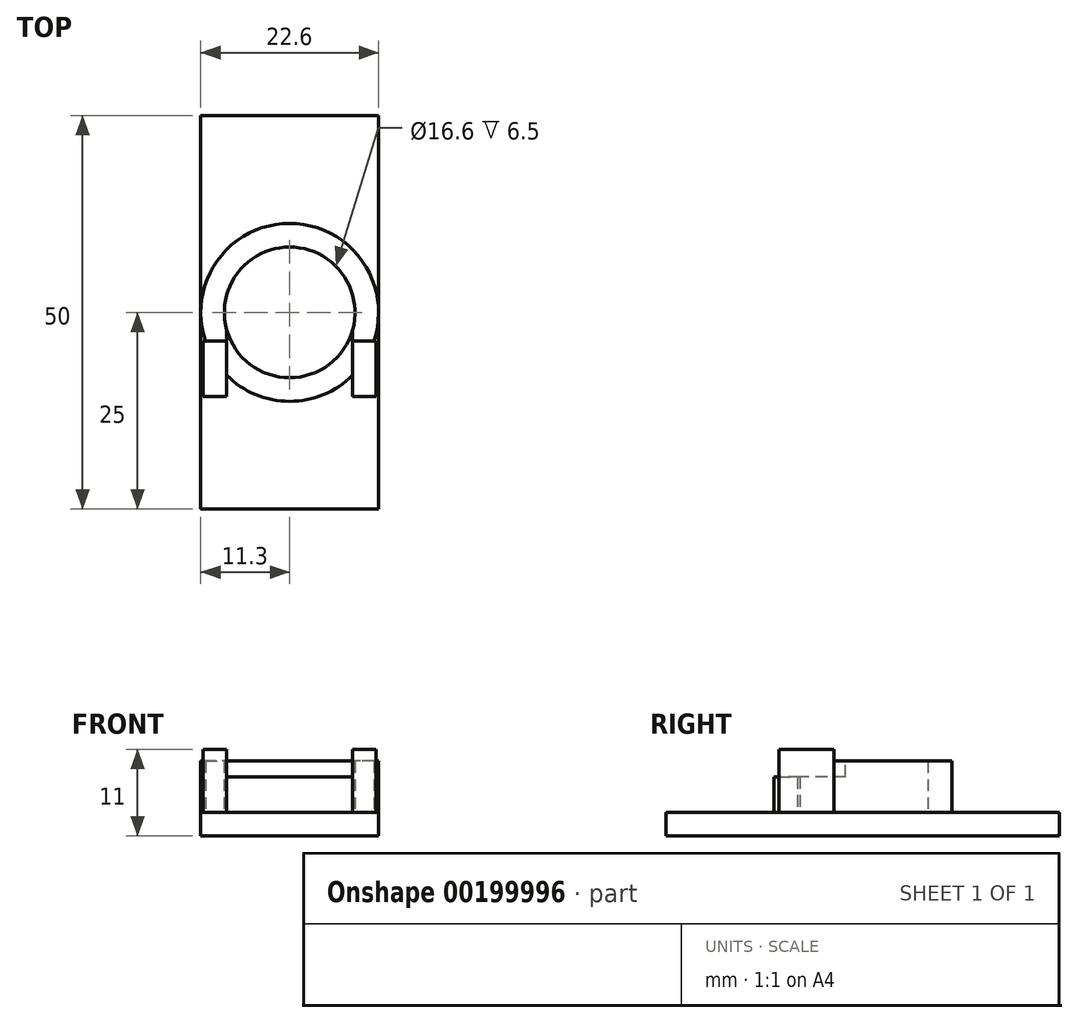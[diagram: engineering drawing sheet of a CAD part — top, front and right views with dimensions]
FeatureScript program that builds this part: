
annotation { "Feature Type Name" : "Feature", "Feature Type Description" : "" }
export const myFeature = defineFeature(function(context is Context, id is Id, definition is map)
    precondition{}
    {
        {
            var Q0;
            Q0=qCreatedBy(makeId("Top.planeOp"),FACE);
            var sketch = newSketch(context, id + "F0", { "sketchPlane" : qUnion([Q0])});
            skCircle(sketch, "E0", {"center": v(0, 0) * mm, "radius": 8.3 * mm});
            skCircle(sketch, "E1.0", {"center": v(0, 0) * mm, "radius": 11.3 * mm});
            skLineSegment(sketch, "E2.bottom", {"start": v(11.3, 25) * mm, "end": v(-11.3, 25) * mm});
            skLineSegment(sketch, "E2.top", {"start": v(11.3, -25) * mm, "end": v(-11.3, -25) * mm});
            skLineSegment(sketch, "E2.left", {"start": v(11.3, 25) * mm, "end": v(11.3, -25) * mm});
            skLineSegment(sketch, "E2.right", {"start": v(-11.3, 25) * mm, "end": v(-11.3, -25) * mm});
            skLineSegment(sketch, "E3.bottom", {"start": v(-11, -3.67) * mm, "end": v(-8, -3.67) * mm});
            skLineSegment(sketch, "E3.top", {"start": v(-11, -10.67) * mm, "end": v(-8, -10.67) * mm});
            skLineSegment(sketch, "E3.left", {"start": v(-11, -3.67) * mm, "end": v(-11, -10.67) * mm});
            skLineSegment(sketch, "E3.right", {"start": v(-8, -3.67) * mm, "end": v(-8, -10.67) * mm});
            skLineSegment(sketch, "E4", {"start": v(0, 0) * mm, "end": v(0, -25) * mm, "construction": true});
            skLineSegment(sketch, "E5.MirrorCS", {"start": v(11, -3.67) * mm, "end": v(8, -3.67) * mm});
            skLineSegment(sketch, "E6.MirrorCS", {"start": v(8, -3.67) * mm, "end": v(8, -10.67) * mm});
            skLineSegment(sketch, "E7.MirrorCS", {"start": v(11, -3.67) * mm, "end": v(11, -10.67) * mm});
            skLineSegment(sketch, "E8.MirrorCS", {"start": v(11, -10.67) * mm, "end": v(8, -10.67) * mm});
            skPoint(sketch, "E9", {"position": v(0, -11.3) * mm});
            skLineSegment(sketch, "E10", {"start": v(0, 0) * mm, "end": v(11.3, 0) * mm, "construction": true});
            skSolve(sketch);
        }
        {
            var Q0;
            Q0=makeQuery(id+"F0.imprint","IMPRINT",FACE,{"disambiguationData":[TD([[makeQuery(id+"F0.imprint","IMPRINT",EDGE,{"derivedFrom":sQuery(id+"F0.wireOp",EDGE,"E0")}),-1.0]])]});
            extrude(context, id + "F1", {"entities" : qUnion([Q0]), "depth" : 6.5 * mm});
        }
        {
            var Q0;
            {var subQ0=sQuery(id+"F0.wireOp",EDGE,"E6.MirrorCS");var subQ1=sQuery(id+"F0.wireOp",EDGE,"E1.0");var subQ2=makeQuery(id+"F0.imprint","INTERSECT",VERTEX,{"derivedFrom":[subQ1,subQ0]});Q0=makeQuery(id+"F0.imprint","IMPRINT",FACE,{"disambiguationData":[TD([[makeQuery(id+"F0.imprint","IMPRINT",EDGE,{"disambiguationData":[TD([[subQ2,-1.0]])],"derivedFrom":subQ1}),1.0]])]});}
            var Q1;
            {var subQ0=sQuery(id+"F0.wireOp",EDGE,"E7.MirrorCS");Q1=makeQuery(id+"F0.imprint","IMPRINT",FACE,{"disambiguationData":[TD([[makeQuery(id+"F0.imprint","IMPRINT",EDGE,{"derivedFrom":subQ0}),-1.0]])]});}
            var Q2;
            {var subQ0=sQuery(id+"F0.wireOp",EDGE,"E3.top");Q2=makeQuery(id+"F0.imprint","IMPRINT",FACE,{"disambiguationData":[TD([[makeQuery(id+"F0.imprint","IMPRINT",EDGE,{"derivedFrom":subQ0}),1.0]])]});}
            var Q3;
            {var subQ0=sQuery(id+"F0.wireOp",EDGE,"E3.bottom");var subQ1=sQuery(id+"F0.wireOp",EDGE,"E1.0");var subQ2=makeQuery(id+"F0.imprint","INTERSECT",VERTEX,{"derivedFrom":[subQ1,subQ0]});Q3=makeQuery(id+"F0.imprint","IMPRINT",FACE,{"disambiguationData":[TD([[makeQuery(id+"F0.imprint","IMPRINT",EDGE,{"disambiguationData":[TD([[subQ2,-1.0]])],"derivedFrom":subQ1}),1.0]])]});}
            extrude(context, id + "F2", {"entities" : qUnion([Q0, Q1, Q2, Q3]), "operationType" : NewBodyOperationType.ADD, "depth" : 8 * mm});
        }
        {
            var Q0;
            Q0=makeQuery(id+"F1.opExtrude","CAP_FACE",FACE,{"disambiguationData":[OSD([sQuery(id+"F0.wireOp",EDGE,"E0"),sQuery(id+"F0.wireOp",EDGE,"E1.0"),sQuery(id+"F0.wireOp",EDGE,"E3.bottom"),sQuery(id+"F0.wireOp",EDGE,"E3.right"),sQuery(id+"F0.wireOp",EDGE,"E5.MirrorCS"),sQuery(id+"F0.wireOp",EDGE,"E6.MirrorCS")])],"isStart":false});
            var sketch = newSketch(context, id + "F3", { "sketchPlane" : qUnion([Q0])});
            skLineSegment(sketch, "E11.0", {"start": v(-8, -3.67) * mm, "end": v(-8, -10.67) * mm});
            skLineSegment(sketch, "E12.0", {"start": v(8, -3.67) * mm, "end": v(8, -10.67) * mm});
            skLineSegment(sketch, "E13", {"start": v(-8, -10.67) * mm, "end": v(8, -10.67) * mm});
            skLineSegment(sketch, "E14", {"start": v(8, -3.67) * mm, "end": v(-8, -3.67) * mm});
            skLineSegment(sketch, "E15.top", {"start": v(-8, -11.3) * mm, "end": v(8, -11.3) * mm});
            skLineSegment(sketch, "E15.left", {"start": v(-8, -10.67) * mm, "end": v(-8, -11.3) * mm});
            skLineSegment(sketch, "E15.right", {"start": v(8, -10.67) * mm, "end": v(8, -11.3) * mm});
            skPoint(sketch, "E16.0", {"position": v(0, -11.3) * mm});
            skLineSegment(sketch, "E17.top", {"start": v(8, -2.21) * mm, "end": v(-8, -2.21) * mm});
            skLineSegment(sketch, "E17.left", {"start": v(8, -3.67) * mm, "end": v(8, -2.21) * mm});
            skLineSegment(sketch, "E17.right", {"start": v(-8, -3.67) * mm, "end": v(-8, -2.21) * mm});
            skSolve(sketch);
        }
        {
            var Q0;
            {var subQ0=sQuery(id+"F3.wireOp",EDGE,"E14");var subQ1=makeQuery(id+"F1.opExtrude","CAP_EDGE",EDGE,{"disambiguationData":[OSD([sQuery(id+"F0.wireOp",EDGE,"E0")])],"isStart":false});var subQ2=makeQuery(id+"F3.imprint","INTERSECT",VERTEX,{"disambiguationData":[OD(0.0)],"derivedFrom":[subQ1,subQ0]});Q0=makeQuery(id+"F3.imprint","IMPRINT",FACE,{"disambiguationData":[TD([[makeQuery(id+"F3.imprint","IMPRINT",EDGE,{"disambiguationData":[TD([[subQ2,-1.0]])],"derivedFrom":subQ0}),1.0]])]});}
            var Q1;
            {var subQ0=sQuery(id+"F3.wireOp",EDGE,"E14");var subQ3=makeQuery(id+"F1.opExtrude","CAP_EDGE",EDGE,{"disambiguationData":[OSD([sQuery(id+"F0.wireOp",EDGE,"E0")])],"isStart":false});var subQ10=makeQuery(id+"F3.imprint","INTERSECT",VERTEX,{"disambiguationData":[OD(0.0)],"derivedFrom":[subQ3,subQ0]});Q1=makeQuery(id+"F3.imprint","IMPRINT",FACE,{"disambiguationData":[TD([[makeQuery(id+"F3.imprint","IMPRINT",EDGE,{"disambiguationData":[TD([[subQ10,1.0]])],"derivedFrom":subQ3}),-1.0]])]});}
            var Q2;
            {var subQ0=sQuery(id+"F3.wireOp",EDGE,"E12.0");var subQ4=sQuery(id+"F3.wireOp",EDGE,"E13");var subQ5=makeQuery(id+"F3.imprint","INTERSECT",VERTEX,{"derivedFrom":[subQ0,subQ4,sQuery(id+"F3.wireOp",EDGE,"E15.right")]});Q2=makeQuery(id+"F3.imprint","IMPRINT",FACE,{"disambiguationData":[TD([[makeQuery(id+"F3.imprint","IMPRINT",EDGE,{"disambiguationData":[TD([[subQ5,1.0]])],"derivedFrom":subQ0}),-1.0]])]});}
            var Q3;
            {var subQ0=sQuery(id+"F3.wireOp",EDGE,"E11.0");var subQ4=sQuery(id+"F3.wireOp",EDGE,"E13");var subQ5=makeQuery(id+"F3.imprint","INTERSECT",VERTEX,{"derivedFrom":[subQ0,subQ4,sQuery(id+"F3.wireOp",EDGE,"E15.left")]});Q3=makeQuery(id+"F3.imprint","IMPRINT",FACE,{"disambiguationData":[TD([[makeQuery(id+"F3.imprint","IMPRINT",EDGE,{"disambiguationData":[TD([[subQ5,1.0]])],"derivedFrom":subQ0}),1.0]])]});}
            var Q4;
            {var subQ0=sQuery(id+"F3.wireOp",EDGE,"E15.right");Q4=makeQuery(id+"F3.imprint","IMPRINT",FACE,{"disambiguationData":[TD([[makeQuery(id+"F3.imprint","IMPRINT",EDGE,{"derivedFrom":subQ0}),-1.0]])]});}
            var Q5;
            {var subQ0=sQuery(id+"F3.wireOp",EDGE,"E13");var subQ1=sQuery(id+"F0.wireOp",EDGE,"E1.0");var subQ2=makeQuery(id+"F1.opExtrude","CAP_EDGE",EDGE,{"disambiguationData":[OSD([subQ1]),TDD([makeQuery(id+"F0.imprint","IMPRINT",EDGE,{"disambiguationData":[TD([[makeQuery(id+"F0.imprint","INTERSECT",VERTEX,{"derivedFrom":[subQ1,sQuery(id+"F0.wireOp",EDGE,"E3.right")]}),-1.0]])],"derivedFrom":subQ1})])],"isStart":false});var subQ3=makeQuery(id+"F3.imprint","INTERSECT",VERTEX,{"disambiguationData":[OD(0.0)],"derivedFrom":[subQ2,subQ0]});Q5=makeQuery(id+"F3.imprint","IMPRINT",FACE,{"disambiguationData":[TD([[makeQuery(id+"F3.imprint","IMPRINT",EDGE,{"disambiguationData":[TD([[subQ3,-1.0]])],"derivedFrom":subQ0}),-1.0]])]});}
            var Q6;
            {var subQ0=sQuery(id+"F3.wireOp",EDGE,"E15.left");Q6=makeQuery(id+"F3.imprint","IMPRINT",FACE,{"disambiguationData":[TD([[makeQuery(id+"F3.imprint","IMPRINT",EDGE,{"derivedFrom":subQ0}),1.0]])]});}
            var Q7;
            {var subQ1=sQuery(id+"F3.wireOp",EDGE,"E14");var subQ3=makeQuery(id+"F1.opExtrude","CAP_EDGE",EDGE,{"disambiguationData":[OSD([sQuery(id+"F0.wireOp",EDGE,"E0")])],"isStart":false});var subQ4=makeQuery(id+"F3.imprint","INTERSECT",VERTEX,{"disambiguationData":[OD(0.0)],"derivedFrom":[subQ3,subQ1]});Q7=makeQuery(id+"F3.imprint","IMPRINT",FACE,{"disambiguationData":[TD([[makeQuery(id+"F3.imprint","IMPRINT",EDGE,{"disambiguationData":[TD([[subQ4,-1.0]])],"derivedFrom":subQ3}),-1.0]])]});}
            var Q8;
            {var subQ2=sQuery(id+"F3.wireOp",EDGE,"E17.right");Q8=makeQuery(id+"F3.imprint","IMPRINT",FACE,{"disambiguationData":[TD([[makeQuery(id+"F3.imprint","IMPRINT",EDGE,{"derivedFrom":subQ2}),-1.0]])]});}
            var Q9;
            {var subQ0=sQuery(id+"F3.wireOp",EDGE,"E17.top");Q9=makeQuery(id+"F3.imprint","IMPRINT",FACE,{"disambiguationData":[TD([[makeQuery(id+"F3.imprint","IMPRINT",EDGE,{"derivedFrom":subQ0}),1.0]])]});}
            extrude(context, id + "F4", {"entities" : qUnion([Q0, Q1, Q2, Q3, Q4, Q5, Q6, Q7, Q8, Q9]), "operationType" : NewBodyOperationType.REMOVE, "oppositeDirection" : true, "depth" : 2 * mm});
        }
        {
            var Q0;
            Q0=makeQuery(id+"F0.imprint","IMPRINT",FACE,{"disambiguationData":[TD([[makeQuery(id+"F0.imprint","IMPRINT",EDGE,{"derivedFrom":sQuery(id+"F0.wireOp",EDGE,"E0")}),-1.0]])]});
            var Q1;
            {var subQ0=sQuery(id+"F0.wireOp",EDGE,"E6.MirrorCS");var subQ1=sQuery(id+"F0.wireOp",EDGE,"E1.0");var subQ2=makeQuery(id+"F0.imprint","INTERSECT",VERTEX,{"derivedFrom":[subQ1,subQ0]});Q1=makeQuery(id+"F0.imprint","IMPRINT",FACE,{"disambiguationData":[TD([[makeQuery(id+"F0.imprint","IMPRINT",EDGE,{"disambiguationData":[TD([[subQ2,-1.0]])],"derivedFrom":subQ1}),1.0]])]});}
            var Q2;
            {var subQ0=sQuery(id+"F0.wireOp",EDGE,"E7.MirrorCS");Q2=makeQuery(id+"F0.imprint","IMPRINT",FACE,{"disambiguationData":[TD([[makeQuery(id+"F0.imprint","IMPRINT",EDGE,{"derivedFrom":subQ0}),-1.0]])]});}
            var Q3;
            {var subQ0=sQuery(id+"F0.wireOp",EDGE,"E3.bottom");var subQ1=sQuery(id+"F0.wireOp",EDGE,"E1.0");var subQ2=makeQuery(id+"F0.imprint","INTERSECT",VERTEX,{"derivedFrom":[subQ1,subQ0]});Q3=makeQuery(id+"F0.imprint","IMPRINT",FACE,{"disambiguationData":[TD([[makeQuery(id+"F0.imprint","IMPRINT",EDGE,{"disambiguationData":[TD([[subQ2,-1.0]])],"derivedFrom":subQ1}),1.0]])]});}
            var Q4;
            {var subQ0=sQuery(id+"F0.wireOp",EDGE,"E3.top");Q4=makeQuery(id+"F0.imprint","IMPRINT",FACE,{"disambiguationData":[TD([[makeQuery(id+"F0.imprint","IMPRINT",EDGE,{"derivedFrom":subQ0}),1.0]])]});}
            var Q5;
            {var subQ4=sQuery(id+"F0.wireOp",EDGE,"E2.top");Q5=makeQuery(id+"F0.imprint","IMPRINT",FACE,{"disambiguationData":[TD([[makeQuery(id+"F0.imprint","IMPRINT",EDGE,{"derivedFrom":subQ4}),-1.0]])]});}
            var Q6;
            {var subQ5=sQuery(id+"F0.wireOp",EDGE,"E2.bottom");Q6=makeQuery(id+"F0.imprint","IMPRINT",FACE,{"disambiguationData":[TD([[makeQuery(id+"F0.imprint","IMPRINT",EDGE,{"derivedFrom":subQ5}),1.0]])]});}
            var Q7;
            Q7=makeQuery(id+"F0.imprint","IMPRINT",FACE,{"disambiguationData":[TD([[makeQuery(id+"F0.imprint","IMPRINT",EDGE,{"derivedFrom":sQuery(id+"F0.wireOp",EDGE,"E0")}),1.0]])]});
            extrude(context, id + "F5", {"entities" : qUnion([Q0, Q1, Q2, Q3, Q4, Q5, Q6, Q7]), "operationType" : NewBodyOperationType.ADD, "oppositeDirection" : true, "depth" : 3 * mm});
        }
    });
